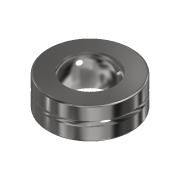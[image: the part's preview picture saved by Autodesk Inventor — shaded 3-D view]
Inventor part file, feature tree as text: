
AUTODESK INVENTOR PART (.ipt)
format: ipt  version: 2021 (Build 250183000, 183)  size: 150,016 bytes
history: native  units: mm (DEFAULTED — no unit token found)
features: other x7, revolve x3, sketch x2
ambient origin geometry x8: Origin, YZ Plane, XZ Plane, XY Plane, X Axis, Y Axis, Z Axis, Center Point
bodies: Solid1 (feature_tree)
feature tree (12):
  sketch  "Sketch_3"  dims[d2=360.0deg]
  revolve  "Revolution1"  Angle=360.0deg
  revolve  "Revolution2"  [1 undecoded]
  revolve  "Revolution3"  [1 undecoded]
  other  "holder_XY"
  other  "holder_YZ"
  other  "holder_ZX"
  other  "holder_X"
  other  "holder_Y"
  other  "holder_Z"
  other  "holder_Center"
  sketch  "Sketch_2"  dims[d0=360.0deg d1=360.0deg]
note: 2 required parameter values undecoded (feature->parameter linkage not recoverable at this tier; creation-order binding heuristic only, values carry confidence <= 0.55)
